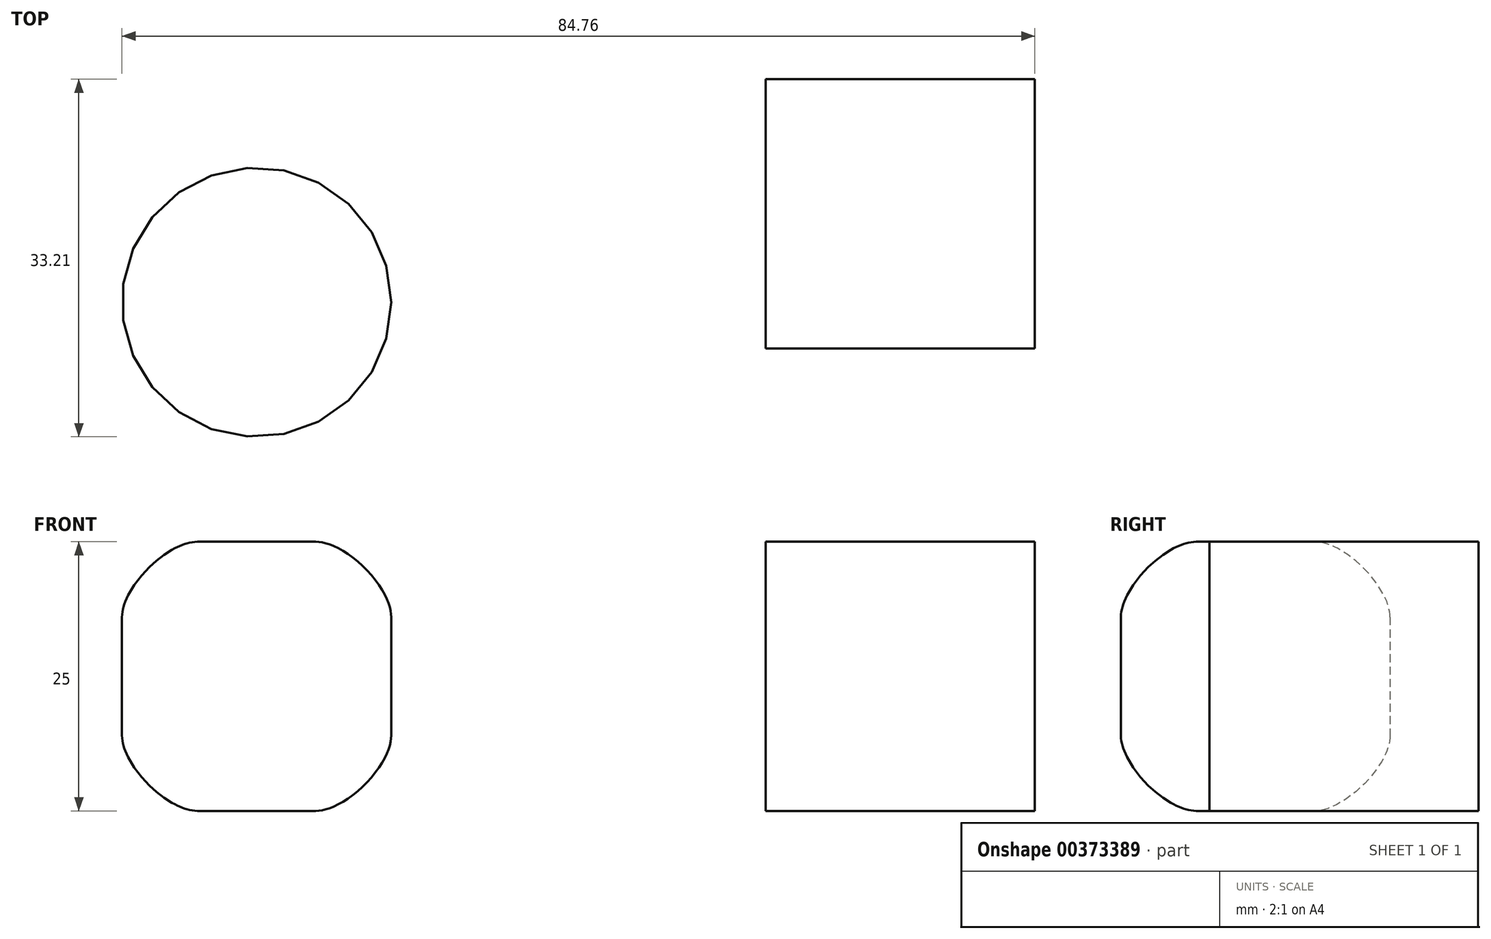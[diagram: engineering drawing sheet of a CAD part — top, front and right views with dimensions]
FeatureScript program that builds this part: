
annotation { "Feature Type Name" : "Feature", "Feature Type Description" : "" }
export const myFeature = defineFeature(function(context is Context, id is Id, definition is map)
    precondition{}
    {
        {
            var Q0;
            Q0=qCreatedBy(makeId("Front.planeOp"),FACE);
            var sketch = newSketch(context, id + "F0", { "sketchPlane" : qUnion([Q0])});
            skLineSegment(sketch, "E0.bottom", {"start": v(0, 0) * mm, "end": v(25, 0) * mm});
            skLineSegment(sketch, "E0.top", {"start": v(0, 25) * mm, "end": v(25, 25) * mm});
            skLineSegment(sketch, "E0.left", {"start": v(0, 0) * mm, "end": v(0, 25) * mm});
            skLineSegment(sketch, "E0.right", {"start": v(25, 0) * mm, "end": v(25, 25) * mm});
            skSolve(sketch);
        }
        {
            var Q0;
            Q0=qSketchRegion(id+"F0",true);
            extrude(context, id + "F1", {"entities" : qUnion([Q0]), "depth" : 25 * mm});
        }
        {
            var Q0;
            Q0=qCreatedBy(makeId("Top.planeOp"),FACE);
            var sketch = newSketch(context, id + "F2", { "sketchPlane" : qUnion([Q0])});
            skCircle(sketch, "E1", {"center": v(-47.26, -20.71) * mm, "radius": 12.5 * mm});
            skSolve(sketch);
        }
        {
            var Q0;
            Q0=qSketchRegion(id+"F2",true);
            extrude(context, id + "F3", {"entities" : qUnion([Q0]), "depth" : 25 * mm});
        }
        {
            var Q0;
            Q0=makeQuery(id+"F3.opExtrude","CAP_EDGE",EDGE,{"disambiguationData":[OSD([sQuery(id+"F2.wireOp",EDGE,"E1")])],"isStart":false});
            var Q1;
            Q1=makeQuery(id+"F3.opExtrude","CAP_EDGE",EDGE,{"disambiguationData":[OSD([sQuery(id+"F2.wireOp",EDGE,"E1")])],"isStart":true});
            fillet(context, id + "F4", {"entities" : qUnion([Q0, Q1]), "radius" : 7 * mm, "tangentPropagation" : true, "rho" : 0.3, "crossSection" : FilletCrossSection.CONIC, "allowEdgeOverflow" : false});
        }
    });
